# Revit family: Boiler-Weil-McLain-Evergreen_Gas_Boiler EVG70
name_source: partatom
category: Mechanical Equipment
revit_build: Autodesk Revit 2015 (Build: 20140606_1530(x64)
units: mm (PartAtom-declared; Revit-internal decimal feet)

## types (4) — shared parameters
Back Casing = Metal - Weil-Mclain - Paint Black
Boiler Water In = 1"
Boiler Water In Radius = 1"
Boiler Water Out = 1"
Boiler Water Out Radius = 1"
Clearance Depth = 1' - 3 1/2"
Depth = 0' - 11"
Description = Evergreen High-Efficiency Condensing Gas Boiler
Feet = Plastic - Weil-Mclain - Plastic - White
Frequency = 60 Hz
Front Casing = Plastic - Weil-McLain - Paint Tan
Gas Connection Radius = 0"
Gas Connection Size = 1"
Height = 2' - 8 7/32"
Manufacturer = Weil-McLain
Manufacturer Fax = 630-560-3769
Phase = 1
Product Documentation Link = https://www.weil-mclain.com
Product Name = Evergreen Gas Boiler
Product Page URL = https://www.weil-mclain.com
URL = https://www.weil-mclain.com
Voltage = 120 V
Warranty = https://www.weil-mclain.com
Width = 1' - 5 1/32"

## per-type parameters (varying)
| type | Air Vent Radius | Model |
| EVG 70 Combustion Air Size 3" | 2" | Evergreen 70 Gas Boiler |
| EVG 70 | 1" | Evergreen 70 Gas Boiler |
| EVG 110 | 2" | Evergreen 110 Gas Boiler |
| EVG 155 | 2" | Evergreen 155 Gas Boiler |

## geometry (parser evidence)
native form markers: Blend x23, Sweep x19
no freeform markers — native parametric forms only
